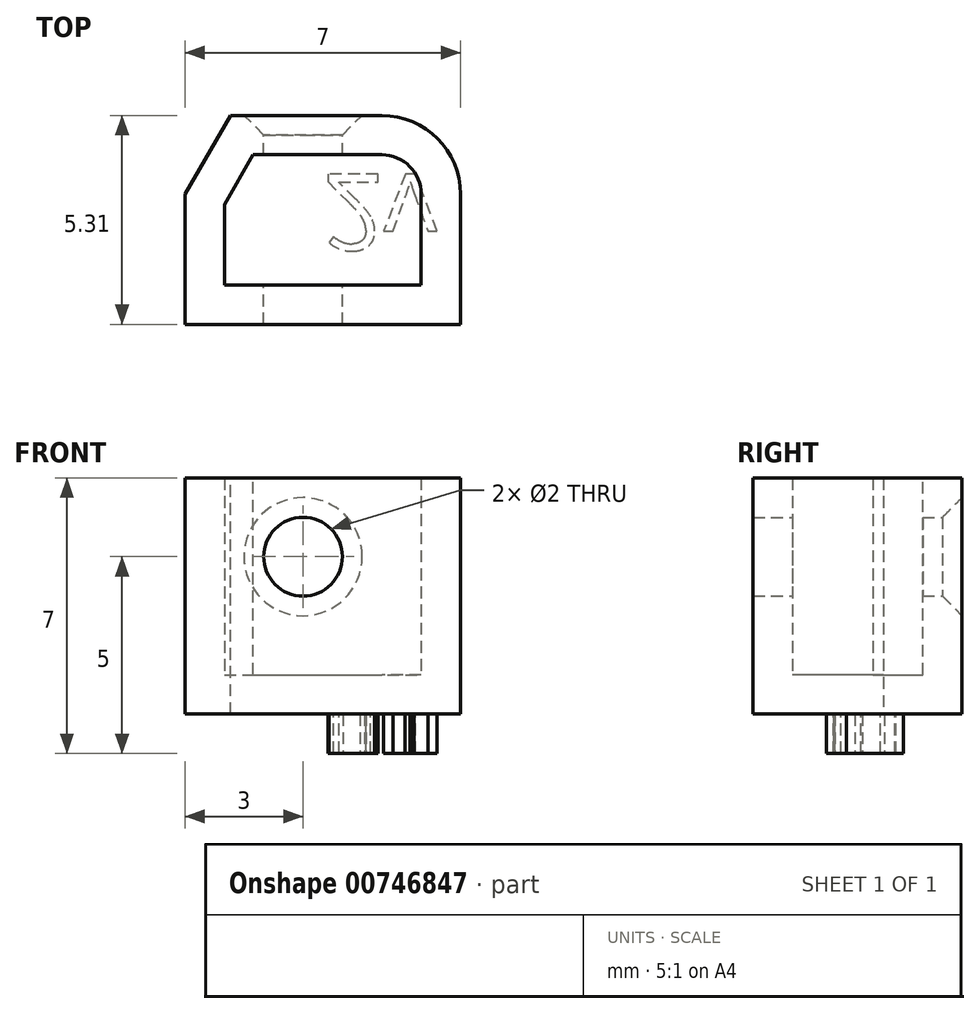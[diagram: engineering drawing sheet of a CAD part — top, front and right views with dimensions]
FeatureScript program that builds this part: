
annotation { "Feature Type Name" : "Feature", "Feature Type Description" : "" }
export const myFeature = defineFeature(function(context is Context, id is Id, definition is map)
    precondition{}
    {
        {
            var Q0;
            Q0=qCreatedBy(makeId("Top.planeOp"),FACE);
            var sketch = newSketch(context, id + "F0", { "sketchPlane" : qUnion([Q0])});
            skLineSegment(sketch, "E0.bottom", {"start": v(-3.5, 5.31) * mm, "end": v(1.5, 5.31) * mm});
            skLineSegment(sketch, "E0.top", {"start": v(-3.5, 0) * mm, "end": v(3.5, 0) * mm});
            skLineSegment(sketch, "E0.left", {"start": v(-3.5, 5.31) * mm, "end": v(-3.5, 0) * mm});
            skLineSegment(sketch, "E0.right", {"start": v(3.5, 3.31) * mm, "end": v(3.5, 0) * mm});
            skPoint(sketch, "E1.visualSharp", {"position": v(3.5, 5.31) * mm});
            skArc(sketch, "E1.filletArc", {"start": v(3.5, 3.31) * mm, "mid": v(2.91, 4.72) * mm, "end": v(1.5, 5.31) * mm});
            skSolve(sketch);
        }
        {
            var Q0;
            Q0=makeQuery(id+"F0.imprint","IMPRINT",FACE,{"disambiguationData":[TD([[makeQuery(id+"F0.imprint","IMPRINT",EDGE,{"derivedFrom":sQuery(id+"F0.wireOp",EDGE,"E0.bottom")}),-1.0]])]});
            extrude(context, id + "F1", {"entities" : qUnion([Q0]), "depth" : 6 * mm, "offsetDistance" : 25 * mm});
        }
        {
            var Q0;
            Q0=makeQuery(id+"F1.opExtrude","SWEPT_EDGE",EDGE,{"disambiguationData":[OSD([sQuery(id+"F0.wireOp",EDGE,"E0.bottom"),sQuery(id+"F0.wireOp",EDGE,"E0.left")])]});
            chamfer(context, id + "F2", {"entities" : qUnion([Q0]), "chamferType" : ChamferType.OFFSET_ANGLE, "width" : 2 * mm, "oppositeDirection" : false, "angle" : 30 * degree, "tangentPropagation" : true});
        }
        {
            var Q0;
            Q0=makeQuery(id+"F1.opExtrude","CAP_FACE",FACE,{"disambiguationData":[OSD([sQuery(id+"F0.wireOp",EDGE,"E0.bottom"),sQuery(id+"F0.wireOp",EDGE,"E0.top"),sQuery(id+"F0.wireOp",EDGE,"E0.left"),sQuery(id+"F0.wireOp",EDGE,"E0.right"),sQuery(id+"F0.wireOp",EDGE,"E1.filletArc")])],"isStart":false});
            shell(context, id + "F3", {"entities" : qUnion([Q0]), "thickness" : 1 * mm});
        }
        {
            var Q0;
            Q0=makeQuery(id+"F1.opExtrude","CAP_FACE",FACE,{"disambiguationData":[OSD([sQuery(id+"F0.wireOp",EDGE,"E0.bottom"),sQuery(id+"F0.wireOp",EDGE,"E0.top"),sQuery(id+"F0.wireOp",EDGE,"E0.left"),sQuery(id+"F0.wireOp",EDGE,"E0.right"),sQuery(id+"F0.wireOp",EDGE,"E1.filletArc")])],"isStart":true});
            var sketch = newSketch(context, id + "F4", { "sketchPlane" : qUnion([Q0])});
            skText(sketch, "E2", { "text": "2v", "fontName": "OpenSans-Regular.ttf"});
            const initialGuessF4  = {"E2": [0, -0.00382, 1, 0, 0.00195]};
            skSetInitialGuess(sketch, initialGuessF4);
            skSolve(sketch);
        }
        {
            var Q0;
            Q0 = qSketchRegion(id + "F4", true);
            extrude(context, id + "F5", {"entities" : qUnion([Q0]), "operationType" : NewBodyOperationType.ADD, "depth" : 1 * mm, "offsetDistance" : 25 * mm});
        }
        {
            var Q0;
            Q0=makeQuery(id+"F1.opExtrude","SWEPT_FACE",FACE,{"disambiguationData":[OSD([sQuery(id+"F0.wireOp",EDGE,"E0.bottom")])]});
            var sketch = newSketch(context, id + "F6", { "sketchPlane" : qUnion([Q0])});
            skPoint(sketch, "E3", {"position": v(0.5, 4) * mm});
            skSolve(sketch);
        }
        {
            var Q0;
            Q0=sQuery(id+"F6.wireOp",VERTEX,"E3");
            var Q1;
            Q1=makeQuery(id+"F1.opExtrude","SWEPT_BODY",BODY,{"disambiguationData":[OSD([sQuery(id+"F0.wireOp",EDGE,"E0.bottom"),sQuery(id+"F0.wireOp",EDGE,"E0.top"),sQuery(id+"F0.wireOp",EDGE,"E0.left"),sQuery(id+"F0.wireOp",EDGE,"E0.right"),sQuery(id+"F0.wireOp",EDGE,"E1.filletArc")])]});
            hole(context, id + "F7", {"style" : HoleStyle.C_SINK, "endStyle" : HoleEndStyle.THROUGH, "holeDiameter" : 2 * mm, "cSinkDiameter" : 3 * mm, "cSinkAngle" : 90 * degree, "majorDiameter" : 5 * mm, "isTappedThrough" : true, "tappedDepth" : 12 * mm, "tapClearance" : 3, "startFromSketch" : true, "locations" : qUnion([Q0]), "scope" : qUnion([Q1])});
        }
    });
